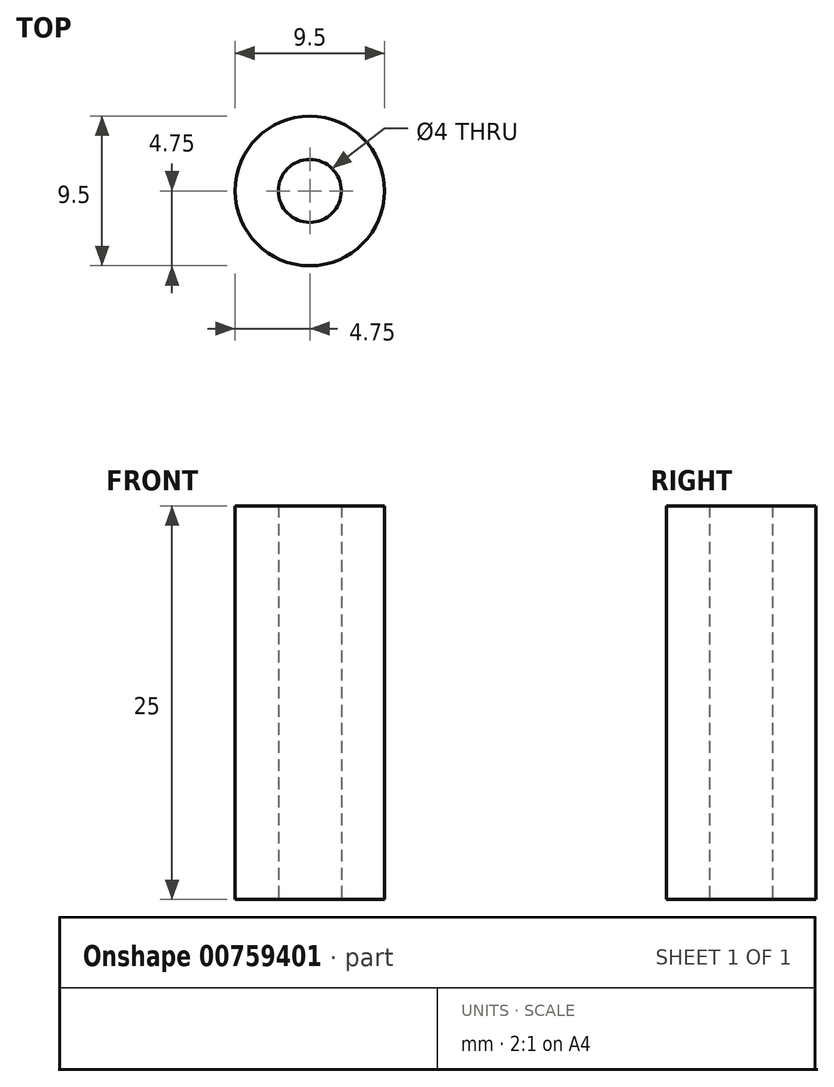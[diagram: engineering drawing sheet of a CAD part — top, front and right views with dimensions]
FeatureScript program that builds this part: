
annotation { "Feature Type Name" : "Feature", "Feature Type Description" : "" }
export const myFeature = defineFeature(function(context is Context, id is Id, definition is map)
    precondition{}
    {
        {
            var Q0;
            Q0=qCreatedBy(makeId("Top.planeOp"),FACE);
            var sketch = newSketch(context, id + "F0", { "sketchPlane" : qUnion([Q0])});
            skCircle(sketch, "E0", {"center": v(0, 0) * mm, "radius": 4.75 * mm});
            skCircle(sketch, "E1", {"center": v(0, 0) * mm, "radius": 2 * mm});
            skSolve(sketch);
        }
        {
            var Q0;
            Q0 = qSketchRegion(id + "F0", true);
            extrude(context, id + "F1", {"entities" : qUnion([Q0]), "depth" : 25 * mm, "offsetDistance" : 25 * mm});
        }
    });
